# Revit family: Showerhead-DXV-Oak_Hill-D35155110_Series
name_source: partatom
category: Plumbing Fixtures
units: mm (PartAtom-declared; Revit-internal decimal feet)

## family parameters
Always vertical = No
Cut with Voids When Loaded = No
OmniClass Number = 23.45.05.14.17
OmniClass Title = Showers
Part Type = Normal
Room Calculation Point = No
Round Connector Dimension = Use Diameter
Shared = Yes
Work Plane-Based = Yes

## types (4) — shared parameters
Assembly Code = D2010710
CEC Compliant = Yes
CW Connection = No
CWFU = 3
CalGreen Compliant = Yes
Default Elevation = 0"
Description = 10" Rain Can Showerhead
Flow Rate = 1.8 GPM (638 L/min)
HW Connection = No
HWFU = 3
Height = 2 25/32"
Installation Type = Shower Arm
Length = 10"
Manufacturer = DXV
Price = Prices may vary. Please consult Manufacturer Representative for most up-to-date price list.
Tempered Water Connection = Yes
Tempered Water Connection Diameter = 1/2"
Tempered Water Connection Radius = 1/4"
URL = https://www.dxv.com
Vent Connection = No
WFU = 4
Waste Connection = No
Width = 10"

## per-type parameters (varying)
| type | Finish | Material |
| D35155110.100 | Brass-DXV-100-Polished Chrome | Brass-DXV-100-Polished Chrome |
| D35155110.144 | Brass-DXV-144-Brushed Nickel | Brass-DXV-144-Brushed Nickel |
| D35155110.150 | Brass-DXV-150-Platinum Nickel | Brass-DXV-150-Platinum Nickel |
| D35155110.427 | Brass-DXV-427-Satin Brass | Brass-DXV-427-Satin Brass |

note: column(s) folded — value = type name in every type: Model

## geometry (parser evidence)
native form markers: Sweep x2
no freeform markers — native parametric forms only
